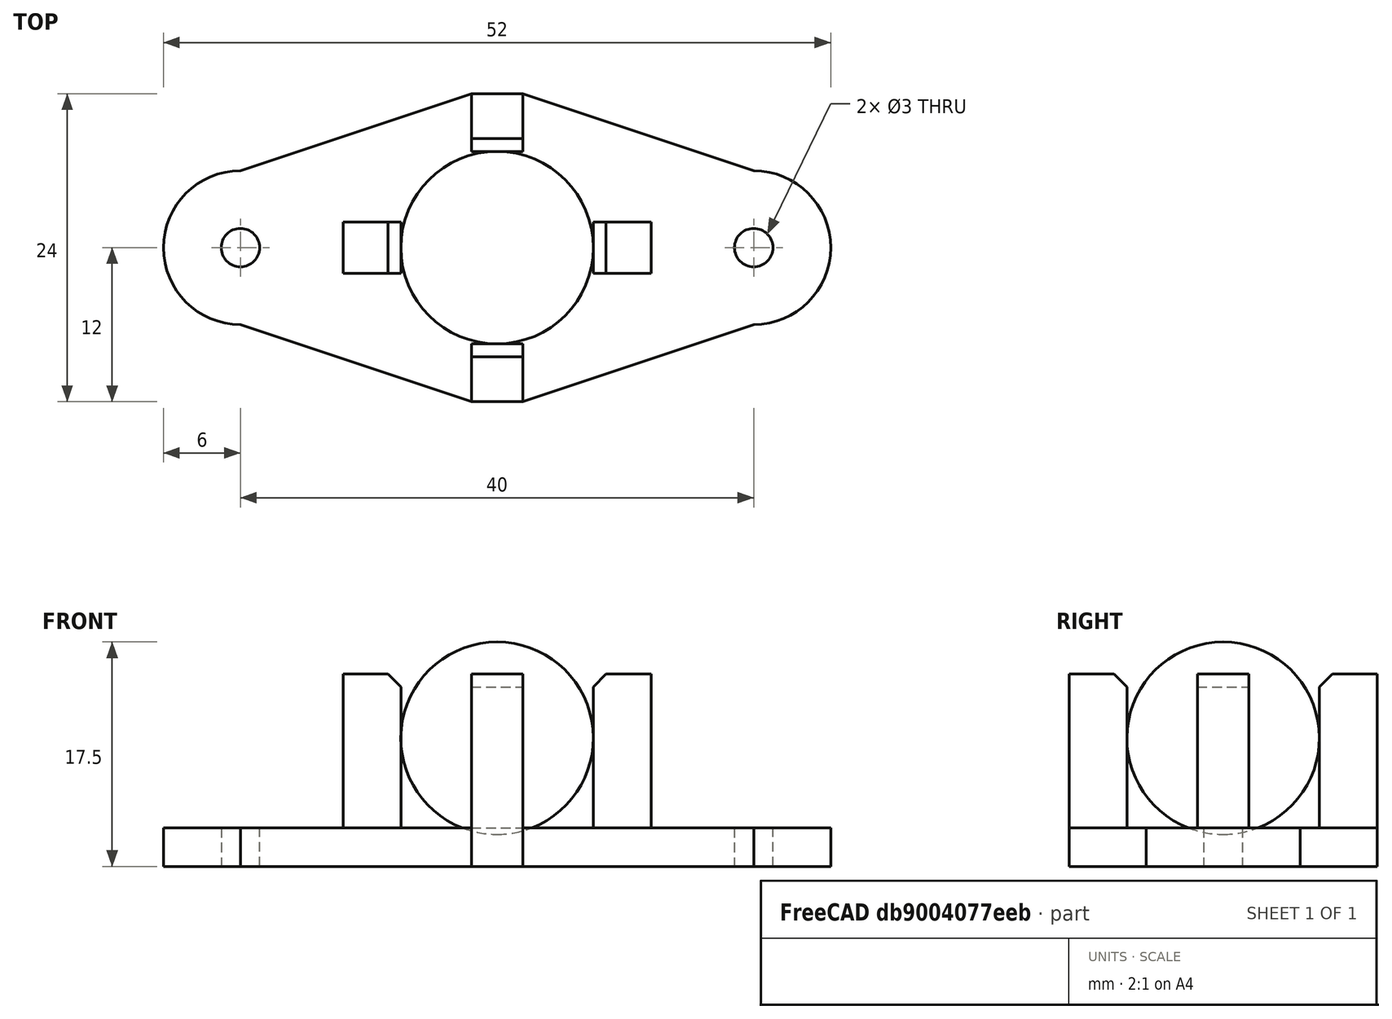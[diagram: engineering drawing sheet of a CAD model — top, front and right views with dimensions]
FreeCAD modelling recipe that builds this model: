
FCSTD DOCUMENT  (FreeCAD 1.0R39109 (Git))
Label: Castor_W420_Steel_Ball
License: All rights reserved
LicenseURL: https://en.wikipedia.org/wiki/All_rights_reserved
objects: Sketcher::SketchObject×2, PartDesign::Pad×2, App::Link×2, Part::Sphere×1, PartDesign::Chamfer×1, PartDesign::Body×1, App::FeaturePython×1, Assembly::JointGroup×1, Assembly::AssemblyObject×1
note: 15 computed .brp shape members not serialized (recipe doc carries the construction recipe); baked Part::Feature solids carry a one-line shape summary decoded from their .brp

FEATURE [Sketcher::SketchObject] Sketch
  ArcFitTolerance = 1e-06
  AttachmentSupport = -> [XY_Plane]
  FullyConstrained = false
  MakeInternals = false
  MapMode = 5
  sketch-geometry (10):
    g0: ArcOfCircle CenterX=20 CenterY=20 CenterZ=0 NormalX=0 NormalY=0 NormalZ=1 AngleXU=0 Radius=6 StartAngle=1.5708 EndAngle=4.71239
    g1: ArcOfCircle CenterX=60 CenterY=20 CenterZ=0 NormalX=0 NormalY=0 NormalZ=1 AngleXU=0 Radius=6 StartAngle=4.71239 EndAngle=7.85398
    g2: LineSegment StartX=20 StartY=26 StartZ=0 EndX=38 EndY=32 EndZ=0
    g3: LineSegment StartX=42 StartY=32 StartZ=0 EndX=60 EndY=26 EndZ=0
    g4: LineSegment StartX=20 StartY=14 StartZ=0 EndX=38 EndY=8 EndZ=0
    g5: LineSegment StartX=42 StartY=8 StartZ=0 EndX=60 EndY=14 EndZ=0
    g6: Circle CenterX=20 CenterY=20 CenterZ=0 NormalX=0 NormalY=0 NormalZ=1 AngleXU=0 Radius=1.5
    g7: Circle CenterX=60 CenterY=20 CenterZ=0 NormalX=0 NormalY=0 NormalZ=1 AngleXU=0 Radius=1.5
    g8: LineSegment StartX=38 StartY=32 StartZ=0 EndX=42 EndY=32 EndZ=0
    g9: LineSegment StartX=38 StartY=8 StartZ=0 EndX=42 EndY=8 EndZ=0
  constraints (19):
    c: Equal(g0,g1)
    c: Diameter(g0) = 12
    c: DistanceX(g0) = 20
    c: DistanceY(g0) = 20
    c: DistanceY(g5,g3) = 24
    c: Coincident(g2,g0)
    c: Coincident(g3,g1)
    c: Coincident(g4,g0)
    c: Coincident(g5,g1)
    c: Coincident(g6,g0)
    c: Coincident(g7,g1)
    c: Diameter(g6) = 3
    c: Equal(g6,g7)
    c: Coincident(g8,g2)
    c: Coincident(g8,g3)
    c: Horizontal(g8)
    c: Coincident(g9,g4)
    c: Coincident(g9,g5)
    c: Horizontal(g9)
FEATURE [PartDesign::Pad] Pad
  Direction = (0,0,1)
  Length = 3
  Length2 = 10
  Profile = -> Sketch
  ReferenceAxis = -> Sketch [N_Axis]
  Refine = true
  Suppressed = false
  Type = 0
FEATURE [Sketcher::SketchObject] Sketch001
  ArcFitTolerance = 1e-06
  AttachmentSupport = -> [Pad]
  FullyConstrained = true
  MakeInternals = false
  MapMode = 5
  Placement = pos=(0,0,3) rot=(0,0,1;0rad)
  sketch-geometry (16):
    g0: LineSegment StartX=38 StartY=32 StartZ=0 EndX=38 EndY=27.5 EndZ=0
    g1: LineSegment StartX=38 StartY=27.5 StartZ=0 EndX=42 EndY=27.5 EndZ=0
    g2: LineSegment StartX=42 StartY=27.5 StartZ=0 EndX=42 EndY=32 EndZ=0
    g3: LineSegment StartX=42 StartY=32 StartZ=0 EndX=38 EndY=32 EndZ=0
    g4: LineSegment StartX=38 StartY=12.5 StartZ=0 EndX=38 EndY=8 EndZ=0
    g5: LineSegment StartX=38 StartY=8 StartZ=0 EndX=42 EndY=8 EndZ=0
    g6: LineSegment StartX=42 StartY=8 StartZ=0 EndX=42 EndY=12.5 EndZ=0
    g7: LineSegment StartX=42 StartY=12.5 StartZ=0 EndX=38 EndY=12.5 EndZ=0
    g8: LineSegment StartX=28 StartY=22 StartZ=0 EndX=28 EndY=18 EndZ=0
    g9: LineSegment StartX=28 StartY=18 StartZ=0 EndX=32.5 EndY=18 EndZ=0
    g10: LineSegment StartX=32.5 StartY=18 StartZ=0 EndX=32.5 EndY=22 EndZ=0
    g11: LineSegment StartX=32.5 StartY=22 StartZ=0 EndX=28 EndY=22 EndZ=0
    g12: LineSegment StartX=47.5 StartY=22 StartZ=0 EndX=47.5 EndY=18 EndZ=0
    g13: LineSegment StartX=47.5 StartY=18 StartZ=0 EndX=52 EndY=18 EndZ=0
    g14: LineSegment StartX=52 StartY=18 StartZ=0 EndX=52 EndY=22 EndZ=0
    g15: LineSegment StartX=52 StartY=22 StartZ=0 EndX=47.5 EndY=22 EndZ=0
  constraints (48):
    c: Coincident(g0,g1)
    c: Coincident(g1,g2)
    c: Coincident(g2,g3)
    c: Coincident(g3,g0)
    c: Vertical(g0)
    c: Vertical(g2)
    c: Horizontal(g1)
    c: Horizontal(g3)
    c: Coincident(g4,g5)
    c: Coincident(g5,g6)
    c: Coincident(g6,g7)
    c: Coincident(g7,g4)
    c: Vertical(g4)
    c: Vertical(g6)
    c: Horizontal(g5)
    c: Horizontal(g7)
    c: Coincident(g8,g9)
    c: Coincident(g9,g10)
    c: Coincident(g10,g11)
    c: Coincident(g11,g8)
    c: Vertical(g8)
    c: Vertical(g10)
    c: Horizontal(g9)
    c: Horizontal(g11)
    c: Coincident(g12,g13)
    c: Coincident(g13,g14)
    c: Coincident(g14,g15)
    c: Coincident(g15,g12)
    c: Vertical(g12)
    c: Vertical(g14)
    c: Horizontal(g13)
    c: Horizontal(g15)
    c: DistanceX(g3,g3) = 4
    c: Equal(g3,g7)
    c: DistanceY(g8,g8) = 4
    c: Equal(g8,g14)
    c: DistanceY(g2,g2) = 4.5
    c: Equal(g2,g6)
    c: DistanceX(g11,g11) = 4.5
    c: Equal(g11,g15)
    c: DistanceX(g4) = 38
    c: DistanceY(g4) = 8
    c: DistanceX(g0) = 38
    c: DistanceY(g0) = 32
    c: DistanceX(g9) = 32.5
    c: DistanceY(g9) = 18
    c: DistanceX(g12) = 47.5
    c: DistanceY(g12) = 18
FEATURE [PartDesign::Pad] Pad001
  BaseFeature = -> Pad
  Direction = (0,0,1)
  Length = 12
  Length2 = 10
  Profile = -> Sketch001
  ReferenceAxis = -> Sketch001 [N_Axis]
  Refine = true
  Suppressed = false
  Type = 0
FEATURE [Part::Sphere] Sphere  label="Steel_Ball"
  Angle1 = -90
  Angle2 = 90
  Angle3 = 360
  AttacherType = Attacher::AttachEngine3D
  Placement = pos=(40,20,10) rot=(0,0,1;0rad)
  Radius = 7.5
FEATURE [PartDesign::Chamfer] Chamfer
  Angle = 45
  Base = -> Pad001 [Edge63,Edge54,Edge47,Edge67]
  BaseFeature = -> Pad001
  ChamferType = 0
  FlipDirection = false
  Refine = true
  Size = 1
  Size2 = 1
  SupportTransform = false
  Suppressed = false
  UseAllEdges = false
FEATURE [PartDesign::Body] Body  label="Plastic_Bracket"
  AllowCompound = false
  Group = -> [Sketch,Pad,Sketch001,Pad001,Chamfer]
  Origin = -> Origin
  Tip = -> Chamfer
FEATURE [App::Link] Plastic_Bracket  label="Plastic_Bracket001"
  LinkPlacement = pos=(60,0,0) rot=(0,0,1;0rad)
  LinkedObject = -> Body
  Placement = pos=(60,0,0) rot=(0,0,1;0rad)
FEATURE [App::Link] Steel_Ball  label="Steel_Ball001"
  LinkPlacement = pos=(100,20,10) rot=(1,0,0;1.5708rad)
  LinkedObject = -> Sphere
  Placement = pos=(100,20,10) rot=(1,0,0;1.5708rad)
FEATURE [App::FeaturePython] GroundedJoint  # Assembly grounded joint (typed FeaturePython)
  ObjectToGround = -> Plastic_Bracket
  Placement = pos=(60,0,0) rot=(0,0,1;0rad)
FEATURE [Assembly::JointGroup] Joints
  Group = -> [GroundedJoint]
FEATURE [Assembly::AssemblyObject] Assembly  label="Castor_Sub_Assembly"
  Group = -> [Joints,Plastic_Bracket,Steel_Ball,GroundedJoint]
  Origin = -> Origin002
  Type = Assembly
